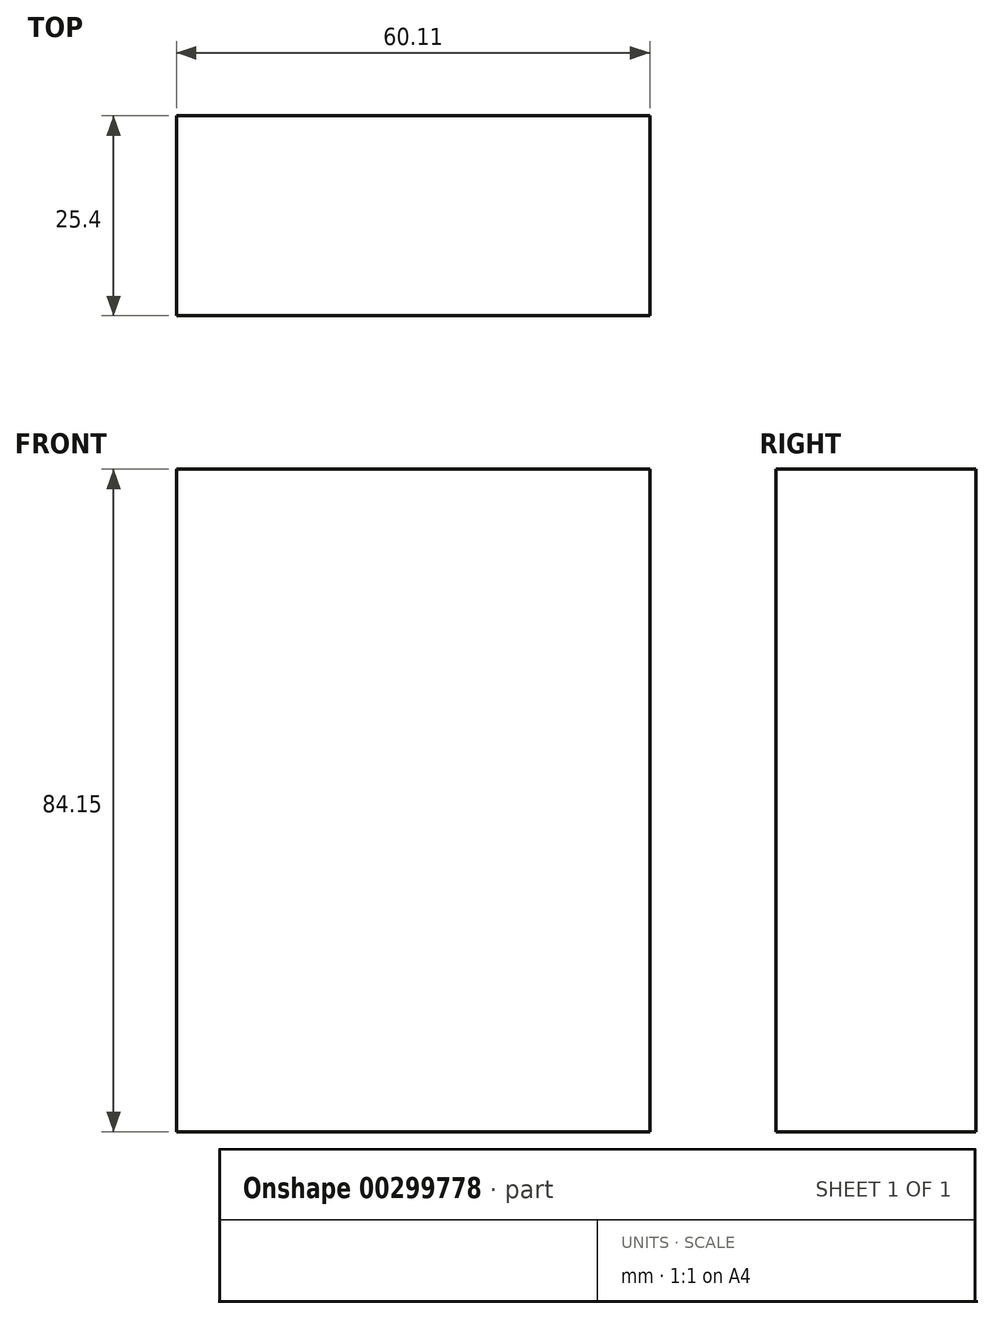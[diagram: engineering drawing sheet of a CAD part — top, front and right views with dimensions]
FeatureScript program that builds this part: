
annotation { "Feature Type Name" : "Feature", "Feature Type Description" : "" }
export const myFeature = defineFeature(function(context is Context, id is Id, definition is map)
    precondition{}
    {
        {
            var Q0;
            Q0=qCreatedBy(makeId("Front.planeOp"),FACE);
            var sketch = newSketch(context, id + "F0", { "sketchPlane" : qUnion([Q0])});
            skLineSegment(sketch, "E0.bottom", {"start": v(-35.87, 44.34) * mm, "end": v(24.24, 44.34) * mm});
            skLineSegment(sketch, "E0.top", {"start": v(-35.87, -39.8) * mm, "end": v(24.24, -39.8) * mm});
            skLineSegment(sketch, "E0.left", {"start": v(-35.87, 44.34) * mm, "end": v(-35.87, -39.8) * mm});
            skLineSegment(sketch, "E0.right", {"start": v(24.24, 44.34) * mm, "end": v(24.24, -39.8) * mm});
            skSolve(sketch);
        }
        {
            var Q0;
            Q0 = qSketchRegion(id + "F0", true);
            extrude(context, id + "F1", {"entities" : qUnion([Q0]), "depth" : 25.4 * mm});
        }
    });
